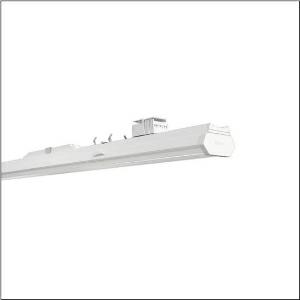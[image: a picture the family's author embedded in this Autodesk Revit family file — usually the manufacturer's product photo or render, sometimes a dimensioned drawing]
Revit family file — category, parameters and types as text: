
# Revit family: licross_r__21_protected_mo_52ts12dne7xf_c152
name_source: partatom
category: Lighting Fixtures
units: mm (PartAtom-declared; Revit-internal decimal feet)

## family parameters
Cut with Voids When Loaded = No
Host = Face
Light Source = No
Part Type = Normal
Room Calculation Point = No
Round Connector Dimension = Use Diameter
Shared = No

## types (1)
- --- (1 x LED, 7250 lm, 60.9 W, 5000K)
    Apparent Load = 61 VA
    CIE Flux Codes = 54 82 95 97 100
    Color Rendering = 90
    Color Temperature = 5000K
    Default Elevation = 1800 mm
    Description = Licross® 21 Protected MO, luminaire insert, of sheet steel, galvanised, coil coated, white, length: 1.500mm, width: 90mm, height: 101mm, LED rated luminous flux: 7.250lm, light colour: 950, control gear: DALI 2, control gear: ECG DALI, with plug, 5-pole, with phase selection, mains connection: 220..240V, AC, 50/60Hz, halogen-free wiring, primary optical cover: cover, of PMMA, light emission: direct with ceiling illumination distribution, protection rating (complete): IP50, insulation class (complete): insulation class I (protective earthing), certification: CE, ENEC, VDE, UKCA, protection symbol: D if used in an environment with non-conductive dust loads with corresponding accessories, permissible ambient temperature for indoor applications: -25..+40°C, corresponds to IFS (International Featured Standards) requirements for safety and quality in the food industry, reducing of maximum allowable ambient temperature of 5°C with ceiling mounting, packaging unit: 1 piece
    Height = 92 mm
    Lamp = 1 x LED
    Lamp Light Flux = 7250 lm
    Lamp Power = 60.9 W
    Lamp count = 1
    Length = 1500 mm
    Luminous efficacy = 119 lm/W
    Manufacturer = Siteco
    ModVariant = No
    Model = 52TS12DNE7XF
    Mounting Place = Ceiling
    Mounting Type = Pendant
    Number of Poles = 1
    OnlyDefault = Yes
    Power Factor = 1
    Product Name = Licross® 21 Protected MO
    Product group = luminaire insert
    ProductGroupID = 902
    Protection Class = Protection class I
    Protection Degree = IP 50
    RLX_Detail_Level = 1
    RlxData = <blob elided: 24189 chars, md5=94cd67ef>
    Socket = socket
    Standby Power = 0 W
    System Light Flux = 7250 lm
    System Power = 61 W
    Type Comments = factory setting: luminous flux: 100 % | dim-lin: 254 | 405 mA
    Type Image = l_1256145.jpg
    URL = http://relux.com
    VarID = @adj_129533
    Voltage = 0 V
    Weight = 0.00 kg
    Width = 88 mm

## geometry (parser evidence)
native form markers: Blend x4, Sweep x10
no freeform markers — native parametric forms only
